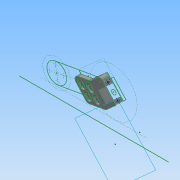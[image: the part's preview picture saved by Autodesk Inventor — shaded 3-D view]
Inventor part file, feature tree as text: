
AUTODESK INVENTOR PART (.ipt)
format: ipt  version: 2014 SP2 (Build 180246200, 246)  size: 405,504 bytes
history: native  units: in
note: dims shown in document units (in); Inventor stores cm internally (conversion verified against a paired STEP export)
features: sketch x7, extrude x6, projected_geometry x6, other x2, hole x2, fillet x1
ambient origin geometry x8: Origin, YZ Plane, XZ Plane, XY Plane, X Axis, Y Axis, Z Axis, Center Point
bodies: Solid1 (feature_tree), Solid2 (feature_tree)
feature tree (24):
  other  "MountSketch.ipt"
  extrude  "Extrusion1"  Depth=0.5in TaperAngle=0.0deg
  extrude  "Extrusion2"  Depth=0.25in
  extrude  "Extrusion4"  Depth=0.5in TaperAngle=0.0deg
  extrude  "Extrusion5"  Depth=0.25in TaperAngle=0.0deg
  fillet  "Fillet1"  Radius=0.36in
  hole  "Hole1"  [1 undecoded]
  extrude  "Extrusion3"  Depth=0.25in TaperAngle=0.0deg
  hole  "Hole3"  [1 undecoded]
  sketch  "Sketch8"  dims[d39=0.25in d40=0.25in d41=0.25in d42=0.25in d43=0.3in]
  extrude  "Cutoff Tabs"  Depth=0.25in
  other  "Axle Centers"
  sketch  "Sketch2"  dims[d0=0.3937in d1=0.5in d2=0.0in]
  sketch  "Sketch3"  dims[d3=0.5in d4=0.0in d5=0.25in]
  sketch  "Sketch4"  dims[d6=0.13in d7=0.75in d8=0.375in d9=0.25in d10=0.5635in d11=0.75in d12=0.8108in d13=0.5in d14=0.0in]
  projected_geometry  "Projected Loop1"
  projected_geometry  "Projected Loop2"
  sketch  "Sketch5"  dims[d22=0.177in d23=0.75in d24=0.119in d25=0.25in d26=0.5635in d27=0.75in d28=0.8108in d29=0.25in d30=0.0in d31=0.36in]
  projected_geometry  "Projected Loop3"
  sketch  "Sketch6"  dims[d32=0.14in d33=0.0in d35=0.25in]
  projected_geometry  "Projected Loop4"
  sketch  "Sketch7"  dims[d36=0.25in d37=0.02in d38=0.0in]
  projected_geometry  "Projected Loop7"
  projected_geometry  "Projected Loop8"
note: 2 required parameter values undecoded (feature->parameter linkage not recoverable at this tier; creation-order binding heuristic only, values carry confidence <= 0.55)
